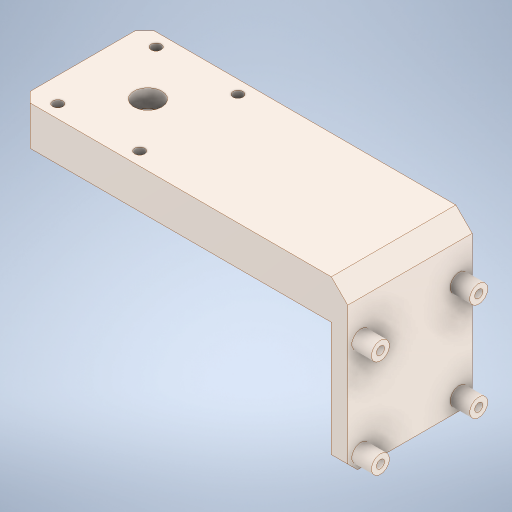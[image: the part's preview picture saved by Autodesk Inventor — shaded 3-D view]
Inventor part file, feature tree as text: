
AUTODESK INVENTOR PART (.ipt)
format: ipt  version: 2023 (Build 270158000, 158)  size: 448,000 bytes
history: mixed  units: mm
features: extrude x9, sketch x8, chamfer x3, fillet x1, plane x1, other x1, imported_body x1
ambient origin geometry x8: Origin, YZ Plane, XZ Plane, XY Plane, X Axis, Y Axis, Z Axis, Center Point
bodies: Solid1 (imported_parasolid)
feature tree (24):
  extrude  "Extrusion1"  Depth=38.0mm
  extrude  "Extrusion2"  Depth=5.0mm TaperAngle=0.0deg
  extrude  "Extrusion3"  Depth=2.5mm
  extrude  "Extrusion4"  Depth=2.5mm
  fillet  "Fillet1"  Radius=4.0mm
  extrude  "Extrusion6"  Depth=5.0mm TaperAngle=0.0deg
  extrude  "Extrusion7"  Depth=5.5mm
  extrude  "Extrusion8"  Depth=5.5mm
  extrude  "Extrusion9"  Depth=5.0mm
  chamfer  "Chamfer1"  Distance=70.0mm
  chamfer  "Chamfer2"  Distance=12.0mm
  chamfer  "Chamfer3"  Distance=100.0mm
  plane  "Work Plane1"
  extrude  "Extrusion10"  Depth=25.0mm
  sketch  "Sketch1"  dims[d0=5.0mm d1=0.0mm d2=38.0mm]
  sketch  "Sketch3"  dims[d3=38.0mm d4=5.0mm d5=0.0mm]
  sketch  "Sketch4"  dims[d6=2.5mm d7=2.5mm]
  sketch  "Sketch7"  dims[d8=2.5mm d9=2.5mm d10=4.0mm]
  sketch  "Sketch9"  dims[d11=4.0mm d12=5.0mm d13=0.0mm]
  sketch  "Sketch10"  dims[d14=5.5mm d15=5.5mm]
  sketch  "Sketch11"  dims[d16=5.5mm d17=5.5mm]
  sketch  "Sketch12"  dims[d18=6.0mm d19=0.0mm d20=5.0mm d23=70.0mm d24=0.0mm d25=12.0mm d26=100.0mm d27=0.0mm d28=25.0mm d29=30.0mm d30=8.5mm d31=3.1mm d32=3.1mm d33=3.1mm d34=3.1mm d35=20.0mm d36=100.0mm d37=0.0mm d38=13.2mm d39=6.5mm d40=0.0mm d41=3.0mm d42=2.0mm d43=45.0deg d44=3.0mm d45=2.0mm d46=45.0deg d47=5.0mm d48=2.0mm d49=45.0deg d50=45.0deg d51=6.5mm d52=0.0mm]
  other  "Boss-Extrude6"
  imported_body  NMx_Import_Brep_tag  [imported B-rep: ~40 faces, bbox_mm=[106.0, 50.0, 38.0]]
